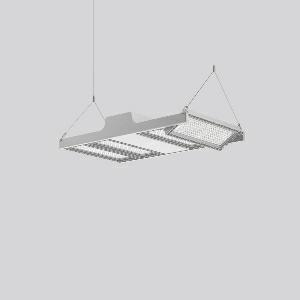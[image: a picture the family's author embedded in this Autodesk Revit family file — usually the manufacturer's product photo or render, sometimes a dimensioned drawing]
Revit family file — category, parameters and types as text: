
# Revit family: light_case_921688_004_76_d0e9
name_source: partatom
category: Lighting Fixtures
units: mm (PartAtom-declared; Revit-internal decimal feet)

## family parameters
Cut with Voids When Loaded = No
Host = Face
Light Source = No
Part Type = Normal
Room Calculation Point = No
Round Connector Dimension = Use Diameter
Shared = No

## types (1)
- LIGHT CASE (1 x LED Modul 840, 8900 lm, 4000)
    Apparent Load = 225 VA
    CIE Flux Codes = 81 98 100 100 100
    Color Rendering = 80
    Color Temperature = 4000
    Default Elevation = 1800 mm
    Description = Series: LIGHT CASE
Flat highbay luminaire for chain or cable suspension with 4 LED modules that can be swivelled. Housing: die cast aluminium and sheet steel, powder-coated. Optimised thermal management thanks to special luminaire design. Self-cleaning heat sink for constant heat dissipation. Cover: plastic (polycarbonate, shockproof), with integrated four-row lens system. LED modules can be swivelled ± 30° for optimum illumination. Suitable for chain or steel cable suspension (to be provided on site). With 5-pin connection terminal (1.5 m). With integrated movement sensor and light sensor for daylight detection on request. Ball impact proof in accordance with DIN 18032-03 (except steel cable suspension). Luminaire with limited surface temperature in accordance with EN 60598-2-24 for use in environments in which a deposit of conductive dust on the luminaire can be expected. 
Colour: silver, matt (approx. RAL 9006)
Length: 680 mm
Width: 397 mm
Height: 110 mm
Lamp: LED
Socket: without socket
Colour temperature: 4000K
Colour rendering index (CRI): 80
System power: 225 W
Rated luminous flux: 35600 lm
Luminous efficiency: 158 lm/W
Control gear: Converter, dimmable, DALI
Protection class: I
Type of protection: IP 65
    Height = 110 mm
    Lamp = 1 x LED Modul 840
    Lamp Light Flux = 8900 lm
    Lamp count = 1
    Length = 680 mm
    Lifetime = 50000 h
    Luminous efficacy = 158 lm/W
    Manufacturer = RZB
    ModVariant = No
    Model = 921688.004.76
    Mounting Place = Ceiling
    Mounting Type = Pendant
    Number of Poles = 1
    OnlyDefault = Yes
    Power Factor = 1
    Product Name = LIGHT CASE
    Product group = Pendant commercial luminaires
    ProductGroupID = 903
    Protection Class = Protection class I
    Protection Degree = IP 65
    RLX_Detail_Level = 1
    RLX_Emergency_Light_Flux = 0 lm
    RLX_Emergency_Type = 0
    RLX_Emergency_Type_DB = No
    RlxData = <blob elided: 27961 chars, md5=49062e17>
    Socket = socket
    Standby Power = 0 W
    System Light Flux = 35600 lm
    System Power = 225 W
    Type Comments = Product without accessories
    Type Image = 921523.004.76.jpg
    URL = http://relux.com
    VarID = ---
    Voltage = 230 V
    Voltage Range = 220-240 V
    Weight = 0.00 kg
    Width = 397 mm

## geometry (parser evidence)
native form markers: Blend x4, Sweep x17
no freeform markers — native parametric forms only
